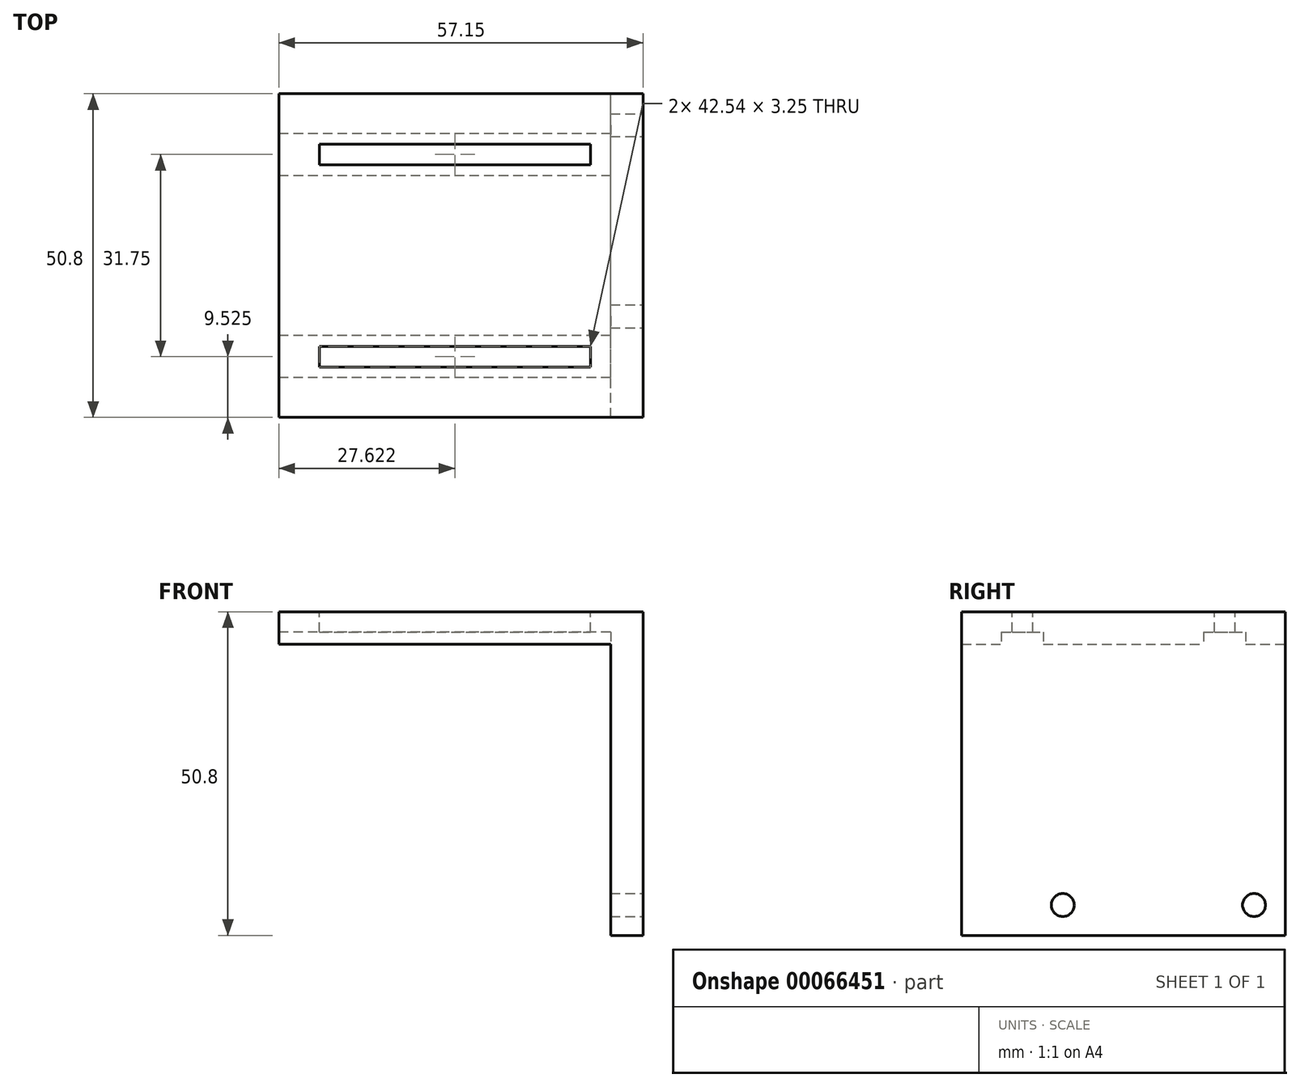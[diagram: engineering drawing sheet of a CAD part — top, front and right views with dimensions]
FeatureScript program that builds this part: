
annotation { "Feature Type Name" : "Feature", "Feature Type Description" : "" }
export const myFeature = defineFeature(function(context is Context, id is Id, definition is map)
    precondition{}
    {
        {
            var Q0;
            Q0=qCreatedBy(makeId("Front.planeOp"),FACE);
            var sketch = newSketch(context, id + "F0", { "sketchPlane" : qUnion([Q0])});
            skLineSegment(sketch, "E0", {"start": v(0, 0) * mm, "end": v(0, 50.8) * mm});
            skLineSegment(sketch, "E1", {"start": v(0, 50.8) * mm, "end": v(-57.15, 50.8) * mm});
            skLineSegment(sketch, "E2", {"start": v(0, 0) * mm, "end": v(-5.08, 0) * mm});
            skLineSegment(sketch, "E3", {"start": v(-5.08, 0) * mm, "end": v(-5.08, 45.72) * mm});
            skLineSegment(sketch, "E4", {"start": v(-5.08, 45.72) * mm, "end": v(-57.15, 45.72) * mm});
            skLineSegment(sketch, "E5", {"start": v(-57.15, 45.72) * mm, "end": v(-57.15, 50.8) * mm});
            skSolve(sketch);
        }
        {
            var Q0;
            Q0 = qSketchRegion(id + "F0", true);
            extrude(context, id + "F1", {"entities" : qUnion([Q0]), "depth" : 50.8 * mm});
        }
        {
            var Q0;
            Q0=makeQuery(id+"F1.opExtrude","SWEPT_FACE",FACE,{"disambiguationData":[OSD([sQuery(id+"F0.wireOp",EDGE,"E0")])]});
            var sketch = newSketch(context, id + "F2", { "sketchPlane" : qUnion([Q0])});
            skCircle(sketch, "E6", {"center": v(-34.93, 4.76) * mm, "radius": 1.8 * mm});
            skCircle(sketch, "E7", {"center": v(-4.93, 4.76) * mm, "radius": 1.8 * mm});
            skSolve(sketch);
        }
        {
            var Q0;
            Q0 = qSketchRegion(id + "F2", true);
            extrude(context, id + "F3", {"entities" : qUnion([Q0]), "operationType" : NewBodyOperationType.REMOVE, "oppositeDirection" : true, "depth" : 25.4 * mm});
        }
        {
            var Q0;
            Q0=makeQuery(id+"F1.opExtrude","SWEPT_FACE",FACE,{"disambiguationData":[OSD([sQuery(id+"F0.wireOp",EDGE,"E1")])]});
            var sketch = newSketch(context, id + "F4", { "sketchPlane" : qUnion([Q0])});
            skLineSegment(sketch, "E8.bottom", {"start": v(-50.8, -42.9) * mm, "end": v(-8.26, -42.9) * mm});
            skLineSegment(sketch, "E8.top", {"start": v(-50.8, -39.65) * mm, "end": v(-8.26, -39.65) * mm});
            skLineSegment(sketch, "E8.left", {"start": v(-50.8, -42.9) * mm, "end": v(-50.8, -39.65) * mm});
            skLineSegment(sketch, "E8.right", {"start": v(-8.26, -42.9) * mm, "end": v(-8.26, -39.65) * mm});
            skLineSegment(sketch, "E9.bottom", {"start": v(-50.8, -11.15) * mm, "end": v(-8.26, -11.15) * mm});
            skLineSegment(sketch, "E9.top", {"start": v(-50.8, -7.9) * mm, "end": v(-8.26, -7.9) * mm});
            skLineSegment(sketch, "E9.left", {"start": v(-50.8, -11.15) * mm, "end": v(-50.8, -7.9) * mm});
            skLineSegment(sketch, "E9.right", {"start": v(-8.26, -11.15) * mm, "end": v(-8.26, -7.9) * mm});
            skPoint(sketch, "E10", {"position": v(-8.26, -41.28) * mm});
            skPoint(sketch, "E11", {"position": v(-8.26, -9.53) * mm});
            skSolve(sketch);
        }
        {
            var Q0;
            Q0 = qSketchRegion(id + "F4", true);
            extrude(context, id + "F5", {"entities" : qUnion([Q0]), "operationType" : NewBodyOperationType.REMOVE, "oppositeDirection" : true, "depth" : 25.4 * mm});
        }
        {
            var Q0;
            Q0=makeQuery(id+"F1.opExtrude","SWEPT_FACE",FACE,{"disambiguationData":[OSD([sQuery(id+"F0.wireOp",EDGE,"E4")])]});
            var sketch = newSketch(context, id + "F6", { "sketchPlane" : qUnion([Q0])});
            skLineSegment(sketch, "E12.bottom", {"start": v(-5.08, 44.58) * mm, "end": v(-57.15, 44.58) * mm});
            skLineSegment(sketch, "E12.top", {"start": v(-5.08, 37.97) * mm, "end": v(-57.15, 37.97) * mm});
            skLineSegment(sketch, "E12.left", {"start": v(-5.08, 44.58) * mm, "end": v(-5.08, 37.97) * mm});
            skLineSegment(sketch, "E12.right", {"start": v(-57.15, 44.58) * mm, "end": v(-57.15, 37.97) * mm});
            skLineSegment(sketch, "E13.bottom", {"start": v(-57.15, 12.83) * mm, "end": v(-5.08, 12.83) * mm});
            skLineSegment(sketch, "E13.top", {"start": v(-57.15, 6.22) * mm, "end": v(-5.08, 6.22) * mm});
            skLineSegment(sketch, "E13.left", {"start": v(-57.15, 12.83) * mm, "end": v(-57.15, 6.22) * mm});
            skLineSegment(sketch, "E13.right", {"start": v(-5.08, 12.83) * mm, "end": v(-5.08, 6.22) * mm});
            skPoint(sketch, "E14", {"position": v(-57.15, 41.28) * mm});
            skPoint(sketch, "E15", {"position": v(-57.15, 9.53) * mm});
            skSolve(sketch);
        }
        {
            var Q0;
            Q0 = qSketchRegion(id + "F6", true);
            extrude(context, id + "F7", {"entities" : qUnion([Q0]), "operationType" : NewBodyOperationType.REMOVE, "oppositeDirection" : true, "depth" : 1.9 * mm});
        }
    });
